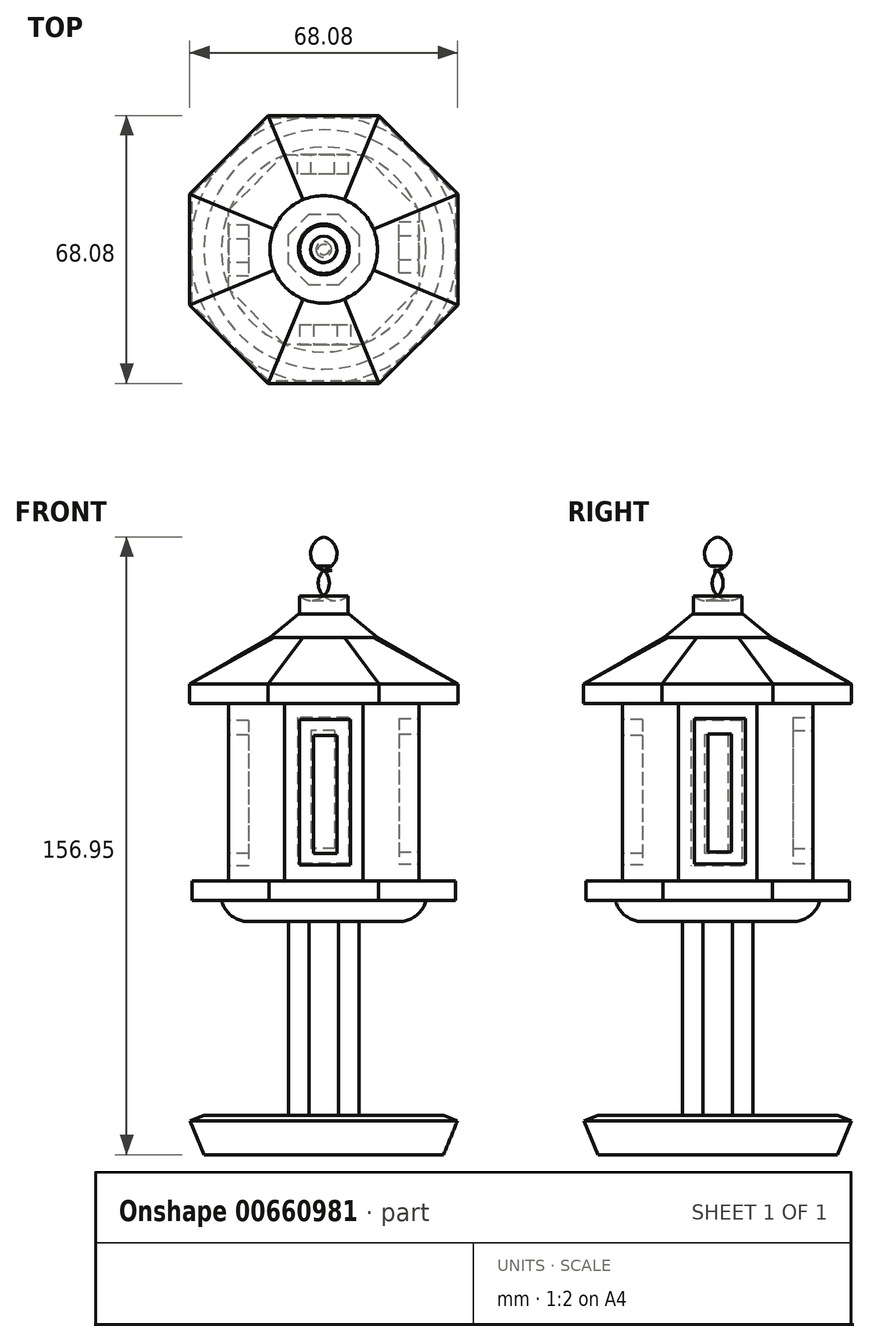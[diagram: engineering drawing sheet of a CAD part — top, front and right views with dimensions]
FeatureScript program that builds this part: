
annotation { "Feature Type Name" : "Feature", "Feature Type Description" : "" }
export const myFeature = defineFeature(function(context is Context, id is Id, definition is map)
    precondition{}
    {
        {
            var Q0;
            Q0=qCreatedBy(makeId("Top.planeOp"),FACE);
            cPlane(context, id + "F0", {"entities" : qUnion([Q0]), "cplaneType" : CPlaneType.OFFSET, "offset" : 10 * mm, "width" : 150 * mm, "height" : 150 * mm});
        }
        {
            var Q0;
            Q0=qCreatedBy(makeId("Top.planeOp"),FACE);
            var sketch = newSketch(context, id + "F1", { "sketchPlane" : qUnion([Q0])});
            skCircle(sketch, "E0", {"center": v(0, 0) * mm, "radius": 42.5 * mm});
            skSolve(sketch);
        }
        {
            var Q0;
            Q0=qCreatedBy(id+"F0.planeOp",FACE);
            var sketch = newSketch(context, id + "F2", { "sketchPlane" : qUnion([Q0])});
            skCircle(sketch, "E1", {"center": v(0, 0) * mm, "radius": 32.5 * mm});
            skSolve(sketch);
        }
        {
            var Q0;
            Q0=makeQuery(id+"F2.imprint","IMPRINT",FACE,{"disambiguationData":[TD([[makeQuery(id+"F2.imprint","IMPRINT",EDGE,{"derivedFrom":sQuery(id+"F2.wireOp",EDGE,"E1")}),1.0]])]});
            var Q1;
            Q1=makeQuery(id+"F1.imprint","IMPRINT",FACE,{"disambiguationData":[TD([[makeQuery(id+"F1.imprint","IMPRINT",EDGE,{"derivedFrom":sQuery(id+"F1.wireOp",EDGE,"E0")}),1.0]])]});
            loft(context, id + "F3", {"sheetProfilesArray" : [{ "sheetProfileEntities" : qUnion([Q0]) }, { "sheetProfileEntities" : qUnion([Q1]) }]});
        }
        {
            var Q0;
            Q0=makeQuery(id+"F3.opLoft","SWEPT_FACE",FACE,{"disambiguationData":[OSD([sQuery(id+"F1.wireOp",EDGE,"E0"),sQuery(id+"F2.wireOp",EDGE,"E1")])]});
            chamfer(context, id + "F4", {"entities" : qUnion([Q0]), "width" : 5 * mm, "tangentPropagation" : true});
        }
        {
            var Q0;
            Q0=makeQuery(id+"F3.opLoft","CAP_FACE",FACE,{"disambiguationData":[OSD([makeQuery(id+"F2.imprint","IMPRINT",FACE,{"disambiguationData":[TD([[makeQuery(id+"F2.imprint","IMPRINT",EDGE,{"derivedFrom":sQuery(id+"F2.wireOp",EDGE,"E1")}),1.0]])]})])],"isStart":true});
            var sketch = newSketch(context, id + "F5", { "sketchPlane" : qUnion([Q0])});
            skCircle(sketch, "E2.cCircle", {"center": v(0, 0) * mm, "radius": 9 * mm, "construction": true});
            skLineSegment(sketch, "E2.0", {"start": v(-3.73, 9) * mm, "end": v(3.73, 9) * mm});
            skLineSegment(sketch, "E2.1", {"start": v(3.73, 9) * mm, "end": v(9, 3.73) * mm});
            skLineSegment(sketch, "E2.2", {"start": v(9, 3.73) * mm, "end": v(9, -3.73) * mm});
            skLineSegment(sketch, "E2.3", {"start": v(9, -3.73) * mm, "end": v(3.73, -9) * mm});
            skLineSegment(sketch, "E2.4", {"start": v(3.73, -9) * mm, "end": v(-3.73, -9) * mm});
            skLineSegment(sketch, "E2.5", {"start": v(-3.73, -9) * mm, "end": v(-9, -3.73) * mm});
            skLineSegment(sketch, "E2.6", {"start": v(-9, -3.73) * mm, "end": v(-9, 3.73) * mm});
            skLineSegment(sketch, "E2.7", {"start": v(-9, 3.73) * mm, "end": v(-3.73, 9) * mm});
            skPoint(sketch, "E2.0.midPoint", {"position": v(0, 9) * mm});
            skSolve(sketch);
        }
        {
            var Q0;
            Q0 = qSketchRegion(id + "F5", true);
            extrude(context, id + "F6", {"entities" : qUnion([Q0]), "operationType" : NewBodyOperationType.ADD, "depth" : 50 * mm, "offsetDistance" : 25 * mm});
        }
        {
            var Q0;
            Q0=qCreatedBy(makeId("Front.planeOp"),FACE);
            var sketch = newSketch(context, id + "F7", { "sketchPlane" : qUnion([Q0])});
            skLineSegment(sketch, "E3", {"start": v(0, 65.96) * mm, "end": v(0, 59.2) * mm});
            skLineSegment(sketch, "E4", {"start": v(0, 59.2) * mm, "end": v(18.95, 59.2) * mm});
            skArc(sketch, "E5", {"start": v(18.95, 59.2) * mm, "mid": v(23.4, 60.7) * mm, "end": v(26.03, 64.59) * mm});
            skLineSegment(sketch, "E6", {"start": v(26.03, 64.59) * mm, "end": v(0, 64.59) * mm});
            skSolve(sketch);
        }
        {
            var Q0;
            {var subQ0=sQuery(id+"F7.wireOp",EDGE,"E4");Q0=makeQuery(id+"F7.imprint","IMPRINT",FACE,{"disambiguationData":[TD([[makeQuery(id+"F7.imprint","IMPRINT",EDGE,{"derivedFrom":subQ0}),1.0]])]});}
            var Q1;
            Q1=sQuery(id+"F7.wireOp",EDGE,"E3");
            revolve(context, id + "F8", {"operationType" : NewBodyOperationType.ADD, "entities" : qUnion([Q0]), "axis" : qUnion([Q1]), "revolveType" : RevolveType.FULL});
        }
        {
            var Q0;
            Q0=makeQuery(id+"F8.opRevolve","SWEPT_FACE",FACE,{"disambiguationData":[OSD([sQuery(id+"F7.wireOp",EDGE,"E6")])]});
            var sketch = newSketch(context, id + "F9", { "sketchPlane" : qUnion([Q0])});
            skCircle(sketch, "E7.cCircle", {"center": v(0, 0) * mm, "radius": 33.5 * mm, "construction": true});
            skLineSegment(sketch, "E7.0", {"start": v(-13.88, 33.5) * mm, "end": v(13.88, 33.5) * mm});
            skLineSegment(sketch, "E7.1", {"start": v(13.88, 33.5) * mm, "end": v(33.5, 13.88) * mm});
            skLineSegment(sketch, "E7.2", {"start": v(33.5, 13.88) * mm, "end": v(33.5, -13.88) * mm});
            skLineSegment(sketch, "E7.3", {"start": v(33.5, -13.88) * mm, "end": v(13.88, -33.5) * mm});
            skLineSegment(sketch, "E7.4", {"start": v(13.88, -33.5) * mm, "end": v(-13.88, -33.5) * mm});
            skLineSegment(sketch, "E7.5", {"start": v(-13.88, -33.5) * mm, "end": v(-33.5, -13.88) * mm});
            skLineSegment(sketch, "E7.6", {"start": v(-33.5, -13.88) * mm, "end": v(-33.5, 13.88) * mm});
            skLineSegment(sketch, "E7.7", {"start": v(-33.5, 13.88) * mm, "end": v(-13.88, 33.5) * mm});
            skPoint(sketch, "E7.0.midPoint", {"position": v(0, 33.5) * mm});
            skSolve(sketch);
        }
        {
            var Q0;
            Q0 = qSketchRegion(id + "F9", true);
            extrude(context, id + "F10", {"entities" : qUnion([Q0]), "operationType" : NewBodyOperationType.ADD, "depth" : 5 * mm, "offsetDistance" : 25 * mm});
        }
        {
            var Q0;
            Q0=makeQuery(id+"F10.opExtrude","CAP_FACE",FACE,{"disambiguationData":[OSD([sQuery(id+"F9.wireOp",EDGE,"E7.0"),sQuery(id+"F9.wireOp",EDGE,"E7.1"),sQuery(id+"F9.wireOp",EDGE,"E7.2"),sQuery(id+"F9.wireOp",EDGE,"E7.3"),sQuery(id+"F9.wireOp",EDGE,"E7.4"),sQuery(id+"F9.wireOp",EDGE,"E7.5"),sQuery(id+"F9.wireOp",EDGE,"E7.6"),sQuery(id+"F9.wireOp",EDGE,"E7.7")])],"isStart":false});
            var sketch = newSketch(context, id + "F11", { "sketchPlane" : qUnion([Q0])});
            skCircle(sketch, "E8.cCircle", {"center": v(0, 0) * mm, "radius": 24.14 * mm, "construction": true});
            skLineSegment(sketch, "E8.0", {"start": v(-10, 24.14) * mm, "end": v(10, 24.14) * mm});
            skLineSegment(sketch, "E8.1", {"start": v(10, 24.14) * mm, "end": v(24.14, 10) * mm});
            skLineSegment(sketch, "E8.2", {"start": v(24.14, 10) * mm, "end": v(24.14, -10) * mm});
            skLineSegment(sketch, "E8.3", {"start": v(24.14, -10) * mm, "end": v(10, -24.14) * mm});
            skLineSegment(sketch, "E8.4", {"start": v(10, -24.14) * mm, "end": v(-10, -24.14) * mm});
            skLineSegment(sketch, "E8.5", {"start": v(-10, -24.14) * mm, "end": v(-24.14, -10) * mm});
            skLineSegment(sketch, "E8.6", {"start": v(-24.14, -10) * mm, "end": v(-24.14, 10) * mm});
            skLineSegment(sketch, "E8.7", {"start": v(-24.14, 10) * mm, "end": v(-10, 24.14) * mm});
            skPoint(sketch, "E8.0.midPoint", {"position": v(0, 24.14) * mm});
            skSolve(sketch);
        }
        {
            var Q0;
            Q0 = qSketchRegion(id + "F11", true);
            extrude(context, id + "F12", {"entities" : qUnion([Q0]), "operationType" : NewBodyOperationType.ADD, "depth" : 45 * mm, "offsetDistance" : 25 * mm});
        }
        {
            var Q0;
            Q0=makeQuery(id+"F12.opExtrude","SWEPT_FACE",FACE,{"disambiguationData":[OSD([sQuery(id+"F11.wireOp",EDGE,"E8.4")])]});
            var sketch = newSketch(context, id + "F13", { "sketchPlane" : qUnion([Q0])});
            skLineSegment(sketch, "E9.bottom", {"start": v(-6.14, 110.58) * mm, "end": v(6.86, 110.58) * mm});
            skLineSegment(sketch, "E9.top", {"start": v(-6.14, 73.58) * mm, "end": v(6.86, 73.58) * mm});
            skLineSegment(sketch, "E9.left", {"start": v(-6.14, 110.58) * mm, "end": v(-6.14, 73.58) * mm});
            skLineSegment(sketch, "E9.right", {"start": v(6.86, 110.58) * mm, "end": v(6.86, 73.58) * mm});
            skLineSegment(sketch, "E10.bottom", {"start": v(-2.64, 106.47) * mm, "end": v(3.36, 106.47) * mm});
            skLineSegment(sketch, "E10.top", {"start": v(-2.64, 76.47) * mm, "end": v(3.36, 76.47) * mm});
            skLineSegment(sketch, "E10.left", {"start": v(-2.64, 106.47) * mm, "end": v(-2.64, 76.47) * mm});
            skLineSegment(sketch, "E10.right", {"start": v(3.36, 106.47) * mm, "end": v(3.36, 76.47) * mm});
            skSolve(sketch);
        }
        {
            var Q0;
            Q0 = qSketchRegion(id + "F13", true);
            extrude(context, id + "F14", {"entities" : qUnion([Q0]), "operationType" : NewBodyOperationType.REMOVE, "oppositeDirection" : true, "depth" : 5 * mm, "offsetDistance" : 25 * mm});
        }
        {
            var Q0;
            Q0=makeQuery(id+"F12.opExtrude","CAP_FACE",FACE,{"disambiguationData":[OSD([sQuery(id+"F11.wireOp",EDGE,"E8.0"),sQuery(id+"F11.wireOp",EDGE,"E8.1"),sQuery(id+"F11.wireOp",EDGE,"E8.2"),sQuery(id+"F11.wireOp",EDGE,"E8.3"),sQuery(id+"F11.wireOp",EDGE,"E8.4"),sQuery(id+"F11.wireOp",EDGE,"E8.5"),sQuery(id+"F11.wireOp",EDGE,"E8.6"),sQuery(id+"F11.wireOp",EDGE,"E8.7")])],"isStart":false});
            var sketch = newSketch(context, id + "F15", { "sketchPlane" : qUnion([Q0])});
            skCircle(sketch, "E11.cCircle", {"center": v(0, 0) * mm, "radius": 34.04 * mm, "construction": true});
            skLineSegment(sketch, "E11.0", {"start": v(-14.1, 34.04) * mm, "end": v(14.1, 34.04) * mm});
            skLineSegment(sketch, "E11.1", {"start": v(14.1, 34.04) * mm, "end": v(34.04, 14.1) * mm});
            skLineSegment(sketch, "E11.2", {"start": v(34.04, 14.1) * mm, "end": v(34.04, -14.1) * mm});
            skLineSegment(sketch, "E11.3", {"start": v(34.04, -14.1) * mm, "end": v(14.1, -34.04) * mm});
            skLineSegment(sketch, "E11.4", {"start": v(14.1, -34.04) * mm, "end": v(-14.1, -34.04) * mm});
            skLineSegment(sketch, "E11.5", {"start": v(-14.1, -34.04) * mm, "end": v(-34.04, -14.1) * mm});
            skLineSegment(sketch, "E11.6", {"start": v(-34.04, -14.1) * mm, "end": v(-34.04, 14.1) * mm});
            skLineSegment(sketch, "E11.7", {"start": v(-34.04, 14.1) * mm, "end": v(-14.1, 34.04) * mm});
            skPoint(sketch, "E11.0.midPoint", {"position": v(0, 34.04) * mm});
            skSolve(sketch);
        }
        {
            var Q0;
            Q0 = qSketchRegion(id + "F15", true);
            extrude(context, id + "F16", {"entities" : qUnion([Q0]), "operationType" : NewBodyOperationType.ADD, "depth" : 5 * mm, "offsetDistance" : 25 * mm});
        }
        {
            var Q0;
            Q0=qCreatedBy(id+"F0.planeOp",FACE);
            cPlane(context, id + "F17", {"entities" : qUnion([Q0]), "cplaneType" : CPlaneType.OFFSET, "offset" : 110 * mm, "width" : 150 * mm, "height" : 150 * mm});
        }
        {
            var Q0;
            Q0=qCreatedBy(id+"F17.planeOp",FACE);
            cPlane(context, id + "F18", {"entities" : qUnion([Q0]), "cplaneType" : CPlaneType.OFFSET, "offset" : 11.4 * mm, "width" : 150 * mm, "height" : 150 * mm});
        }
        {
            var Q0;
            Q0=qCreatedBy(id+"F18.planeOp",FACE);
            var sketch = newSketch(context, id + "F19", { "sketchPlane" : qUnion([Q0])});
            skCircle(sketch, "E12", {"center": v(0, 0) * mm, "radius": 13.66 * mm});
            skSolve(sketch);
        }
        {
            var Q1;
            Q1=makeQuery(id+"F19.imprint","IMPRINT",FACE,{"disambiguationData":[TD([[makeQuery(id+"F19.imprint","IMPRINT",EDGE,{"derivedFrom":sQuery(id+"F19.wireOp",EDGE,"E12")}),1.0]])]});
            var Q2;
            Q2=makeQuery(id+"F16.opExtrude","CAP_FACE",FACE,{"disambiguationData":[OSD([sQuery(id+"F15.wireOp",EDGE,"E11.0"),sQuery(id+"F15.wireOp",EDGE,"E11.1"),sQuery(id+"F15.wireOp",EDGE,"E11.2"),sQuery(id+"F15.wireOp",EDGE,"E11.3"),sQuery(id+"F15.wireOp",EDGE,"E11.4"),sQuery(id+"F15.wireOp",EDGE,"E11.5"),sQuery(id+"F15.wireOp",EDGE,"E11.6"),sQuery(id+"F15.wireOp",EDGE,"E11.7")])],"isStart":false});
            loft(context, id + "F20", {"operationType" : NewBodyOperationType.ADD, "sheetProfilesArray" : [{ "sheetProfileEntities" : qUnion([Q1]) }, { "sheetProfileEntities" : qUnion([Q2]) }]});
        }
        {
            var Q0;
            Q0=qCreatedBy(id+"F18.planeOp",FACE);
            cPlane(context, id + "F21", {"entities" : qUnion([Q0]), "cplaneType" : CPlaneType.OFFSET, "offset" : 6 * mm, "width" : 150 * mm, "height" : 150 * mm});
        }
        {
            var Q0;
            Q0=qCreatedBy(id+"F21.planeOp",FACE);
            var sketch = newSketch(context, id + "F22", { "sketchPlane" : qUnion([Q0])});
            skCircle(sketch, "E13", {"center": v(0, 0) * mm, "radius": 6.44 * mm});
            skSolve(sketch);
        }
        {
            var Q1;
            Q1=makeQuery(id+"F22.imprint","IMPRINT",FACE,{"disambiguationData":[TD([[makeQuery(id+"F22.imprint","IMPRINT",EDGE,{"derivedFrom":sQuery(id+"F22.wireOp",EDGE,"E13")}),1.0]])]});
            var Q2;
            Q2=makeQuery(id+"F20.opLoft","CAP_FACE",FACE,{"disambiguationData":[OSD([makeQuery(id+"F19.imprint","IMPRINT",FACE,{"disambiguationData":[TD([[makeQuery(id+"F19.imprint","IMPRINT",EDGE,{"derivedFrom":sQuery(id+"F19.wireOp",EDGE,"E12")}),1.0]])]})])],"isStart":true});
            loft(context, id + "F23", {"operationType" : NewBodyOperationType.ADD, "sheetProfilesArray" : [{ "sheetProfileEntities" : qUnion([Q1]) }, { "sheetProfileEntities" : qUnion([Q2]) }]});
        }
        {
            var Q0;
            Q0=qCreatedBy(id+"F21.planeOp",FACE);
            var sketch = newSketch(context, id + "F24", { "sketchPlane" : qUnion([Q0])});
            skCircle(sketch, "E14", {"center": v(0, 0) * mm, "radius": 6.1 * mm});
            skSolve(sketch);
        }
        {
            var Q0;
            Q0 = qSketchRegion(id + "F24", true);
            extrude(context, id + "F25", {"entities" : qUnion([Q0]), "operationType" : NewBodyOperationType.ADD, "depth" : 5 * mm, "offsetDistance" : 25 * mm});
        }
        {
            var Q0;
            Q0=qCreatedBy(makeId("Front.planeOp"),FACE);
            var sketch = newSketch(context, id + "F26", { "sketchPlane" : qUnion([Q0])});
            skLineSegment(sketch, "E15", {"start": v(0, 156.95) * mm, "end": v(0, 141.97) * mm});
            skArc(sketch, "E16", {"start": v(0, 156.95) * mm, "mid": v(-3.34, 152.7) * mm, "end": v(0, 148.46) * mm});
            skArc(sketch, "E17", {"start": v(0, 148.46) * mm, "mid": v(-7.49, 145.22) * mm, "end": v(0, 141.97) * mm});
            skSolve(sketch);
        }
        {
            var Q0;
            {var subQ0=sQuery(id+"F26.wireOp",EDGE,"E17");var subQ1=sQuery(id+"F26.wireOp",EDGE,"E15");var subQ2=makeQuery(id+"F26.imprint","INTERSECT",VERTEX,{"derivedFrom":[subQ1,subQ0]});Q0=makeQuery(id+"F26.imprint","IMPRINT",FACE,{"disambiguationData":[TD([[makeQuery(id+"F26.imprint","IMPRINT",EDGE,{"disambiguationData":[TD([[subQ2,1.0]])],"derivedFrom":subQ0}),1.0]])]});}
            var Q1;
            {var subQ0=sQuery(id+"F26.wireOp",EDGE,"E16");var subQ1=sQuery(id+"F26.wireOp",EDGE,"E15");var subQ2=makeQuery(id+"F26.imprint","INTERSECT",VERTEX,{"derivedFrom":[subQ1,subQ0]});Q1=makeQuery(id+"F26.imprint","IMPRINT",FACE,{"disambiguationData":[TD([[makeQuery(id+"F26.imprint","IMPRINT",EDGE,{"disambiguationData":[TD([[subQ2,-1.0]])],"derivedFrom":subQ0}),1.0]])]});}
            var Q2;
            Q2=sQuery(id+"F26.wireOp",EDGE,"E15");
            revolve(context, id + "F27", {"operationType" : NewBodyOperationType.ADD, "entities" : qUnion([Q0, Q1]), "axis" : qUnion([Q2]), "revolveType" : RevolveType.FULL});
        }
        {
            var Q0;
            Q0=makeQuery(id+"F12.opExtrude","SWEPT_FACE",FACE,{"disambiguationData":[OSD([sQuery(id+"F11.wireOp",EDGE,"E8.2")])]});
            var sketch = newSketch(context, id + "F28", { "sketchPlane" : qUnion([Q0])});
            skLineSegment(sketch, "E18.bottom", {"start": v(-5.92, 110.84) * mm, "end": v(7.08, 110.84) * mm});
            skLineSegment(sketch, "E18.top", {"start": v(-5.92, 73.84) * mm, "end": v(7.08, 73.84) * mm});
            skLineSegment(sketch, "E18.left", {"start": v(-5.92, 110.84) * mm, "end": v(-5.92, 73.84) * mm});
            skLineSegment(sketch, "E18.right", {"start": v(7.08, 110.84) * mm, "end": v(7.08, 73.84) * mm});
            skLineSegment(sketch, "E19.bottom", {"start": v(-2.53, 106.9) * mm, "end": v(3.47, 106.9) * mm});
            skLineSegment(sketch, "E19.top", {"start": v(-2.53, 76.9) * mm, "end": v(3.47, 76.9) * mm});
            skLineSegment(sketch, "E19.left", {"start": v(-2.53, 106.9) * mm, "end": v(-2.53, 76.9) * mm});
            skLineSegment(sketch, "E19.right", {"start": v(3.47, 106.9) * mm, "end": v(3.47, 76.9) * mm});
            skSolve(sketch);
        }
        {
            var Q0;
            Q0 = qSketchRegion(id + "F28", true);
            extrude(context, id + "F29", {"entities" : qUnion([Q0]), "operationType" : NewBodyOperationType.REMOVE, "oppositeDirection" : true, "depth" : 5 * mm, "offsetDistance" : 25 * mm});
        }
        {
            var Q0;
            Q0=makeQuery(id+"F12.opExtrude","SWEPT_FACE",FACE,{"disambiguationData":[OSD([sQuery(id+"F11.wireOp",EDGE,"E8.6")])]});
            var sketch = newSketch(context, id + "F30", { "sketchPlane" : qUnion([Q0])});
            skLineSegment(sketch, "E20.bottom", {"start": v(-6.17, 110.34) * mm, "end": v(6.83, 110.34) * mm});
            skLineSegment(sketch, "E20.top", {"start": v(-6.17, 73.34) * mm, "end": v(6.83, 73.34) * mm});
            skLineSegment(sketch, "E20.left", {"start": v(-6.17, 110.34) * mm, "end": v(-6.17, 73.34) * mm});
            skLineSegment(sketch, "E20.right", {"start": v(6.83, 110.34) * mm, "end": v(6.83, 73.34) * mm});
            skLineSegment(sketch, "E21.bottom", {"start": v(-2.67, 106.59) * mm, "end": v(3.33, 106.59) * mm});
            skLineSegment(sketch, "E21.top", {"start": v(-2.67, 76.59) * mm, "end": v(3.33, 76.59) * mm});
            skLineSegment(sketch, "E21.left", {"start": v(-2.67, 106.59) * mm, "end": v(-2.67, 76.59) * mm});
            skLineSegment(sketch, "E21.right", {"start": v(3.33, 106.59) * mm, "end": v(3.33, 76.59) * mm});
            skSolve(sketch);
        }
        {
            var Q0;
            Q0 = qSketchRegion(id + "F30", true);
            extrude(context, id + "F31", {"entities" : qUnion([Q0]), "operationType" : NewBodyOperationType.REMOVE, "oppositeDirection" : true, "depth" : 5 * mm, "offsetDistance" : 25 * mm});
        }
        {
            var Q0;
            Q0=makeQuery(id+"F12.opExtrude","SWEPT_FACE",FACE,{"disambiguationData":[OSD([sQuery(id+"F11.wireOp",EDGE,"E8.0")])]});
            var sketch = newSketch(context, id + "F32", { "sketchPlane" : qUnion([Q0])});
            skLineSegment(sketch, "E22.bottom", {"start": v(-6.3, 111.01) * mm, "end": v(6.7, 111.01) * mm});
            skLineSegment(sketch, "E22.top", {"start": v(-6.3, 74.01) * mm, "end": v(6.7, 74.01) * mm});
            skLineSegment(sketch, "E22.left", {"start": v(-6.3, 111.01) * mm, "end": v(-6.3, 74.01) * mm});
            skLineSegment(sketch, "E22.right", {"start": v(6.7, 111.01) * mm, "end": v(6.7, 74.01) * mm});
            skLineSegment(sketch, "E23.bottom", {"start": v(-2.8, 107.8) * mm, "end": v(3.2, 107.8) * mm});
            skLineSegment(sketch, "E23.top", {"start": v(-2.8, 77.8) * mm, "end": v(3.2, 77.8) * mm});
            skLineSegment(sketch, "E23.left", {"start": v(-2.8, 107.8) * mm, "end": v(-2.8, 77.8) * mm});
            skLineSegment(sketch, "E23.right", {"start": v(3.2, 107.8) * mm, "end": v(3.2, 77.8) * mm});
            skSolve(sketch);
        }
        {
            var Q0;
            Q0 = qSketchRegion(id + "F32", true);
            extrude(context, id + "F33", {"entities" : qUnion([Q0]), "operationType" : NewBodyOperationType.REMOVE, "oppositeDirection" : true, "depth" : 5 * mm, "offsetDistance" : 25 * mm});
        }
    });
